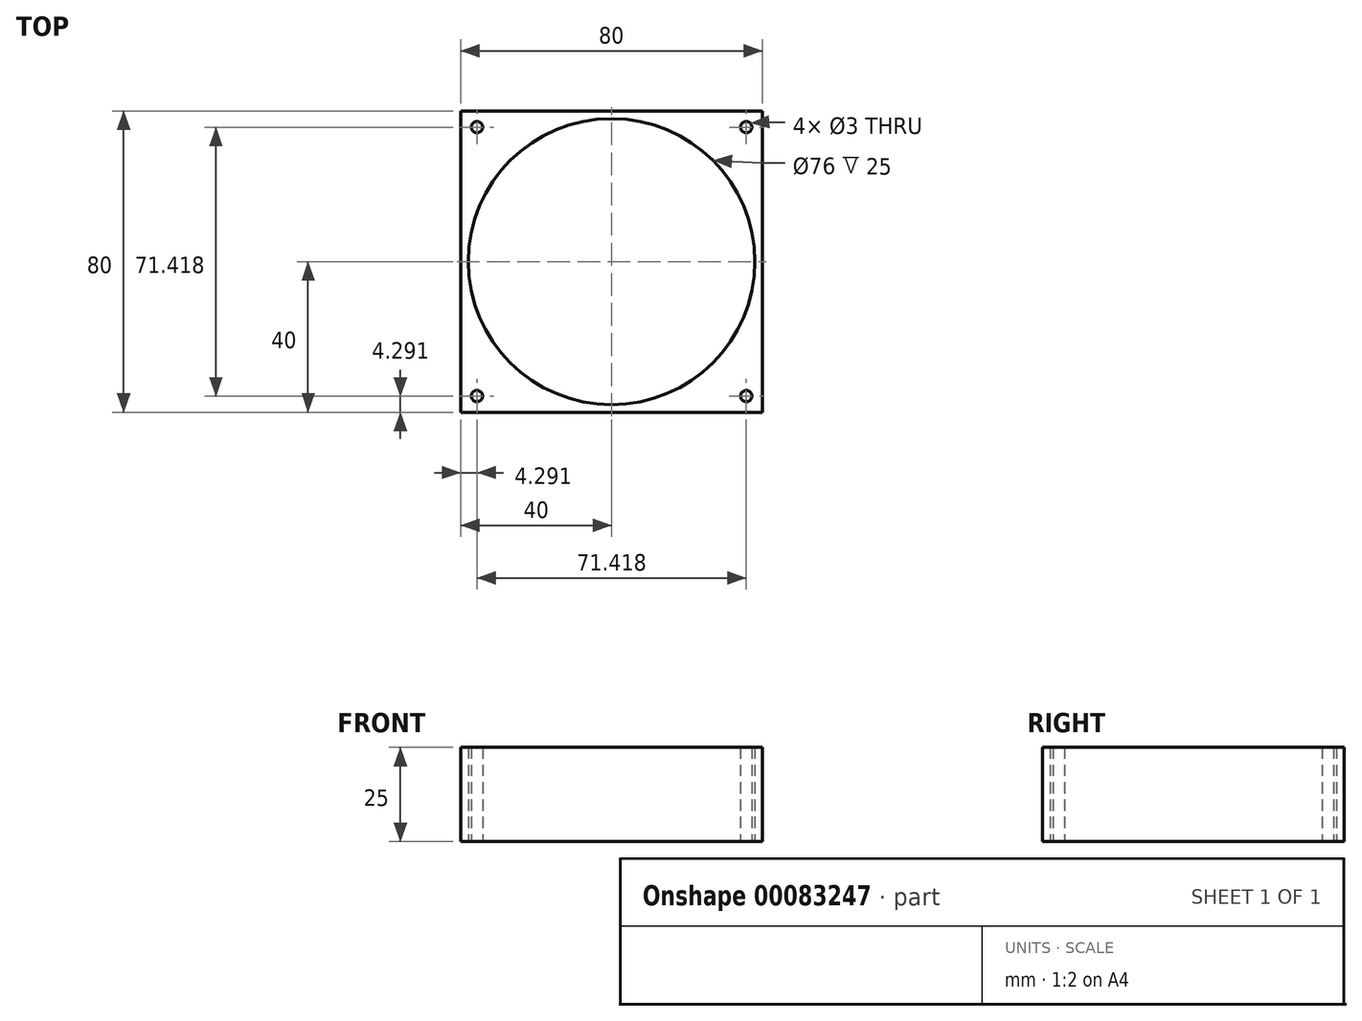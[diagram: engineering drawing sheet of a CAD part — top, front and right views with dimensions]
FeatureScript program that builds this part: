
annotation { "Feature Type Name" : "Feature", "Feature Type Description" : "" }
export const myFeature = defineFeature(function(context is Context, id is Id, definition is map)
    precondition{}
    {
        {
            var Q0;
            Q0=qCreatedBy(makeId("Top.planeOp"),FACE);
            var sketch = newSketch(context, id + "F0", { "sketchPlane" : qUnion([Q0])});
            skCircle(sketch, "E0", {"center": v(0, 0) * mm, "radius": 38 * mm});
            skLineSegment(sketch, "E1.bottom", {"start": v(40, 40) * mm, "end": v(-40, 40) * mm});
            skLineSegment(sketch, "E1.top", {"start": v(40, -40) * mm, "end": v(-40, -40) * mm});
            skLineSegment(sketch, "E1.left", {"start": v(40, 40) * mm, "end": v(40, -40) * mm});
            skLineSegment(sketch, "E1.right", {"start": v(-40, 40) * mm, "end": v(-40, -40) * mm});
            skLineSegment(sketch, "E2", {"start": v(-40, 40) * mm, "end": v(40, -40) * mm, "construction": true});
            skLineSegment(sketch, "E3", {"start": v(40, 40) * mm, "end": v(-40, -40) * mm, "construction": true});
            skCircle(sketch, "E4", {"center": v(0, 0) * mm, "radius": 50.5 * mm, "construction": true});
            skCircle(sketch, "E5", {"center": v(-35.7, 35.7) * mm, "radius": 1.5 * mm});
            skCircle(sketch, "E6", {"center": v(35.7, 35.7) * mm, "radius": 1.5 * mm});
            skCircle(sketch, "E7", {"center": v(-35.7, -35.7) * mm, "radius": 1.5 * mm});
            skCircle(sketch, "E8", {"center": v(35.7, -35.7) * mm, "radius": 1.5 * mm});
            skSolve(sketch);
        }
        {
            var Q0;
            Q0=makeQuery(id+"F0.imprint","IMPRINT",FACE,{"disambiguationData":[TD([[makeQuery(id+"F0.imprint","IMPRINT",EDGE,{"derivedFrom":sQuery(id+"F0.wireOp",EDGE,"E0")}),-1.0]])]});
            extrude(context, id + "F1", {"entities" : qUnion([Q0]), "depth" : 25 * mm});
        }
    });
